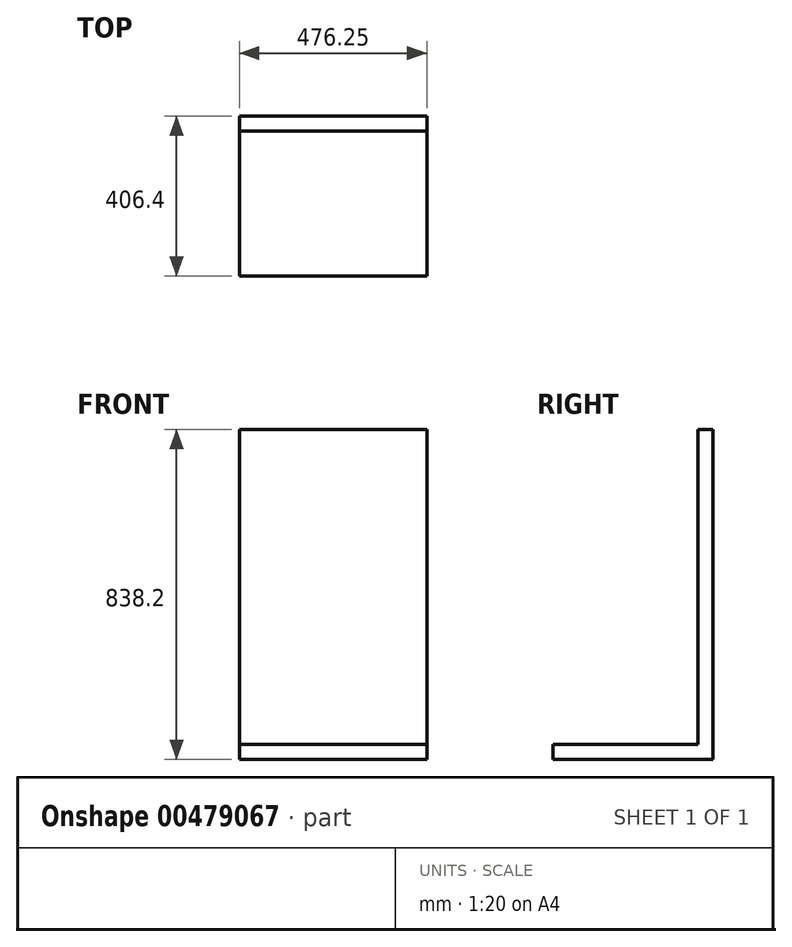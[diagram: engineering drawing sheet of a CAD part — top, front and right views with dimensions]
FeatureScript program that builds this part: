
annotation { "Feature Type Name" : "Feature", "Feature Type Description" : "" }
export const myFeature = defineFeature(function(context is Context, id is Id, definition is map)
    precondition{}
    {
        {
            var Q0;
            Q0=qCreatedBy(makeId("Right.planeOp"),FACE);
            var sketch = newSketch(context, id + "F0", { "sketchPlane" : qUnion([Q0])});
            skLineSegment(sketch, "E0", {"start": v(0, 0) * mm, "end": v(-406.4, 0) * mm});
            skLineSegment(sketch, "E1", {"start": v(-406.4, 0) * mm, "end": v(-406.4, 38.1) * mm});
            skLineSegment(sketch, "E2", {"start": v(-406.4, 38.1) * mm, "end": v(-38.1, 38.1) * mm});
            skLineSegment(sketch, "E3", {"start": v(0, 0) * mm, "end": v(0, 838.2) * mm});
            skLineSegment(sketch, "E4", {"start": v(0, 838.2) * mm, "end": v(-38.1, 838.2) * mm});
            skLineSegment(sketch, "E5", {"start": v(-38.1, 838.2) * mm, "end": v(-38.1, 38.1) * mm});
            skSolve(sketch);
        }
        {
            var Q0;
            Q0=makeQuery(id+"F0.imprint","IMPRINT",FACE,{"disambiguationData":[TD([[makeQuery(id+"F0.imprint","IMPRINT",EDGE,{"derivedFrom":sQuery(id+"F0.wireOp",EDGE,"E0")}),-1.0]])]});
            extrude(context, id + "F1", {"entities" : qUnion([Q0]), "depth" : 476.25 * mm});
        }
    });
